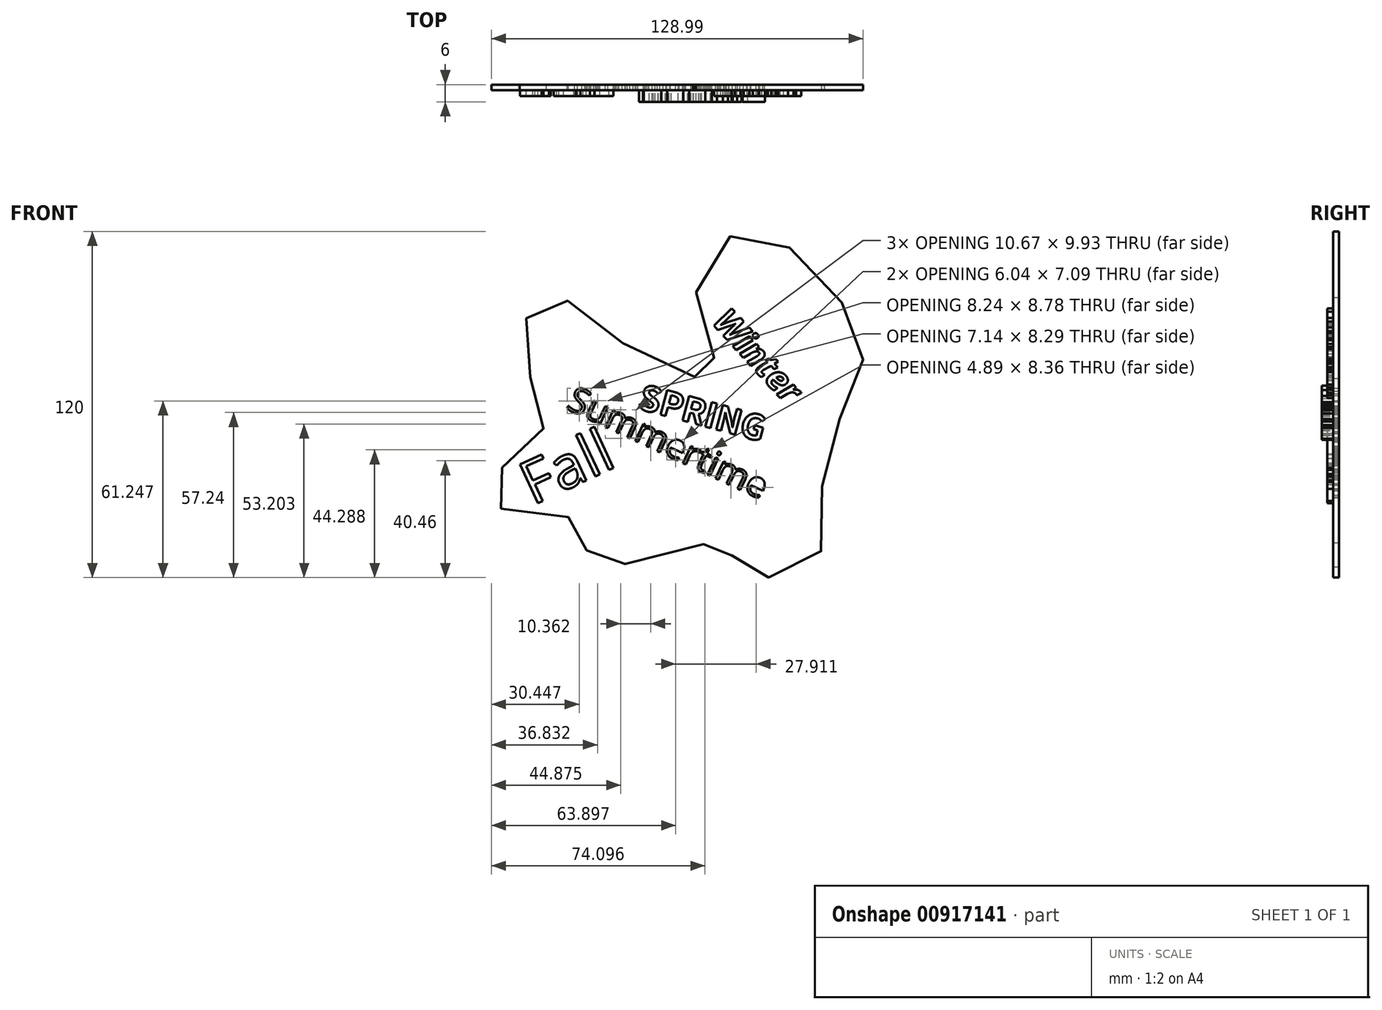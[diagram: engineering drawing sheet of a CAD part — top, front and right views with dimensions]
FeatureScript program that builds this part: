
annotation { "Feature Type Name" : "Feature", "Feature Type Description" : "" }
export const myFeature = defineFeature(function(context is Context, id is Id, definition is map)
    precondition{}
    {
        {
            var Q0;
            Q0=qCreatedBy(makeId("Front.planeOp"),FACE);
            var sketch = newSketch(context, id + "F0", { "sketchPlane" : qUnion([Q0])});
            skFitSpline(sketch, "E0", {"points": [v(-53.3, -34.85) * mm, v(-23.49, -40.4) * mm, v(-22.98, -53.54) * mm, v(15.4, -47.48) * mm, v(25.5, -48.5) * mm, v(31.57, -57.08) * mm, v(56.32, -52.03) * mm, v(58.34, -19.2) * mm, v(71.98, 13.64) * mm, v(61.37, 41.42) * mm, v(30.56, 61.12) * mm, v(14.4, 35.86) * mm, v(21.47, 11.62) * mm, v(-8.33, 20.7) * mm, v(-35.61, 38.39) * mm, v(-46.72, 21.22) * mm, v(-37.63, -4.55) * mm, v(-53.8, -21.72) * mm, v(-53.3, -34.85) * mm]});
            skText(sketch, "E1", { "text": "Summertime\n", "fontName": "OpenSans-Regular.ttf"});
            skPoint(sketch, "E2.0", {"position": v(-6.14, 13.5) * mm});
            const initialGuessF0  = {"E1": [-0.031, 0, 0.9063, -0.42262, 0.00885]};
            skSetInitialGuess(sketch, initialGuessF0);
            skSolve(sketch);
        }
        {
            var Q0;
            Q0=qCreatedBy(makeId("Front.planeOp"),FACE);
            var sketch = newSketch(context, id + "F1", { "sketchPlane" : qUnion([Q0])});
            skText(sketch, "E3", { "text": "Winter\n", "fontName": "OpenSans-BoldItalic.ttf"});
            const initialGuessF1  = {"E3": [0.01965, 0.02968, 0.67395, -0.73878, 0.00872]};
            skSetInitialGuess(sketch, initialGuessF1);
            skSolve(sketch);
        }
        {
            var Q0;
            Q0 = qSketchRegion(id + "F0", true);
            extrude(context, id + "F2", {"entities" : qUnion([Q0]), "depth" : 2 * mm, "offsetDistance" : 25 * mm});
        }
        {
            var Q0;
            Q0 = qSketchRegion(id + "F1", true);
            extrude(context, id + "F3", {"entities" : qUnion([Q0]), "operationType" : NewBodyOperationType.ADD, "depth" : 4 * mm, "offsetDistance" : 25 * mm});
        }
        {
            var Q0;
            Q0=qCreatedBy(makeId("Front.planeOp"),FACE);
            var sketch = newSketch(context, id + "F4", { "sketchPlane" : qUnion([Q0])});
            skText(sketch, "E4", { "text": "Fall", "fontName": "OpenSans-Regular.ttf"});
            const initialGuessF4  = {"E4": [-0.04228, -0.03373, 0.9063, 0.42262, 0.0149]};
            skSetInitialGuess(sketch, initialGuessF4);
            skSolve(sketch);
        }
        {
            var Q0;
            Q0 = qSketchRegion(id + "F4", true);
            extrude(context, id + "F5", {"entities" : qUnion([Q0]), "operationType" : NewBodyOperationType.ADD, "depth" : 4 * mm, "offsetDistance" : 25 * mm});
        }
        {
            var Q0;
            Q0=qCreatedBy(makeId("Front.planeOp"),FACE);
            var sketch = newSketch(context, id + "F6", { "sketchPlane" : qUnion([Q0])});
            skText(sketch, "E5", { "text": "SPRING", "fontName": "NotoSansCJKjp-Bold.otf"});
            const initialGuessF6  = {"E5": [-0.00614, 0, 0.96593, -0.25882, 0.00857]};
            skSetInitialGuess(sketch, initialGuessF6);
            skSolve(sketch);
        }
        {
            var Q0;
            Q0 = qSketchRegion(id + "F6", true);
            extrude(context, id + "F7", {"entities" : qUnion([Q0]), "operationType" : NewBodyOperationType.ADD, "depth" : 6 * mm, "offsetDistance" : 25 * mm});
        }
    });
